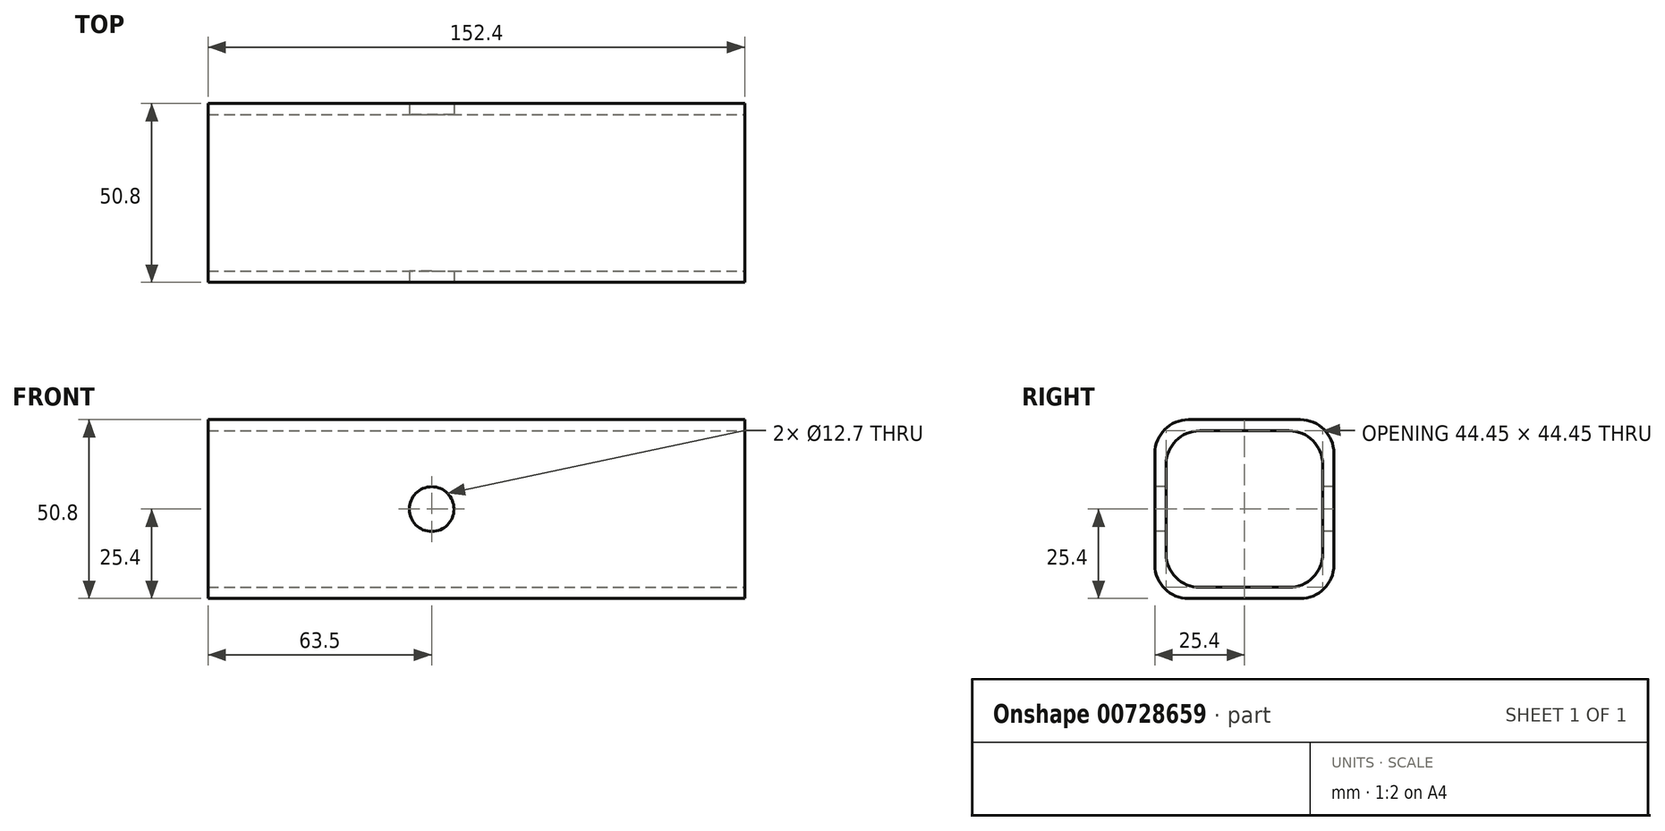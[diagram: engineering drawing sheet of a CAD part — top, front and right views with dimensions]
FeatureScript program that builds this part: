
annotation { "Feature Type Name" : "Feature", "Feature Type Description" : "" }
export const myFeature = defineFeature(function(context is Context, id is Id, definition is map)
    precondition{}
    {
        {
            var Q0;
            Q0=qCreatedBy(makeId("Right.planeOp"),FACE);
            var sketch = newSketch(context, id + "F0", { "sketchPlane" : qUnion([Q0])});
            skLineSegment(sketch, "E0.bottom", {"start": v(0, 0) * mm, "end": v(50.8, 0) * mm});
            skLineSegment(sketch, "E0.top", {"start": v(0, 50.8) * mm, "end": v(50.8, 50.8) * mm});
            skLineSegment(sketch, "E0.left", {"start": v(0, 0) * mm, "end": v(0, 50.8) * mm});
            skLineSegment(sketch, "E0.right", {"start": v(50.8, 0) * mm, "end": v(50.8, 50.8) * mm});
            skSolve(sketch);
        }
        {
            var Q0;
            Q0=qSketchRegion(id+"F0",true);
            extrude(context, id + "F1", {"entities" : qUnion([Q0]), "oppositeDirection" : true, "depth" : 152.4 * mm, "offsetDistance" : 25.4 * mm});
        }
        {
            var Q0;
            Q0=makeQuery(id+"F1.opExtrude","CAP_FACE",FACE,{"disambiguationData":[OSD([sQuery(id+"F0.wireOp",EDGE,"E0.bottom"),sQuery(id+"F0.wireOp",EDGE,"E0.top"),sQuery(id+"F0.wireOp",EDGE,"E0.left"),sQuery(id+"F0.wireOp",EDGE,"E0.right")])],"isStart":true});
            var sketch = newSketch(context, id + "F2", { "sketchPlane" : qUnion([Q0])});
            skLineSegment(sketch, "E1.0", {"start": v(3.17, 47.63) * mm, "end": v(47.63, 47.63) * mm});
            skLineSegment(sketch, "E1.1", {"start": v(3.17, 3.17) * mm, "end": v(3.17, 47.63) * mm});
            skLineSegment(sketch, "E1.2", {"start": v(3.17, 3.17) * mm, "end": v(47.63, 3.17) * mm});
            skLineSegment(sketch, "E1.3", {"start": v(47.63, 3.17) * mm, "end": v(47.63, 47.63) * mm});
            skSolve(sketch);
        }
        {
            var Q0;
            Q0=qSketchRegion(id+"F2",true);
            extrude(context, id + "F3", {"entities" : qUnion([Q0]), "operationType" : NewBodyOperationType.REMOVE, "oppositeDirection" : true, "depth" : 876.3 * mm, "offsetDistance" : 25.4 * mm});
        }
        {
            var Q0;
            Q0=makeQuery(id+"F3.boolean.opBoolean","COPY",EDGE,{"derivedFrom":makeQuery(id+"F3.opExtrude","SWEPT_EDGE",EDGE,{"disambiguationData":[OSD([sQuery(id+"F2.wireOp",EDGE,"E1.1"),sQuery(id+"F2.wireOp",EDGE,"E1.2")])]})});
            var Q1;
            Q1=makeQuery(id+"F3.boolean.opBoolean","COPY",EDGE,{"derivedFrom":makeQuery(id+"F3.opExtrude","SWEPT_EDGE",EDGE,{"disambiguationData":[OSD([sQuery(id+"F2.wireOp",EDGE,"E1.2"),sQuery(id+"F2.wireOp",EDGE,"E1.3")])]})});
            var Q2;
            Q2=makeQuery(id+"F3.boolean.opBoolean","COPY",EDGE,{"derivedFrom":makeQuery(id+"F3.opExtrude","SWEPT_EDGE",EDGE,{"disambiguationData":[OSD([sQuery(id+"F2.wireOp",EDGE,"E1.0"),sQuery(id+"F2.wireOp",EDGE,"E1.3")])]})});
            var Q3;
            Q3=makeQuery(id+"F3.boolean.opBoolean","COPY",EDGE,{"derivedFrom":makeQuery(id+"F3.opExtrude","SWEPT_EDGE",EDGE,{"disambiguationData":[OSD([sQuery(id+"F2.wireOp",EDGE,"E1.0"),sQuery(id+"F2.wireOp",EDGE,"E1.1")])]})});
            var Q4;
            Q4=makeQuery(id+"F1.opExtrude","SWEPT_EDGE",EDGE,{"disambiguationData":[OSD([sQuery(id+"F0.wireOp",EDGE,"E0.bottom"),sQuery(id+"F0.wireOp",EDGE,"E0.right")])]});
            var Q5;
            Q5=makeQuery(id+"F1.opExtrude","SWEPT_EDGE",EDGE,{"disambiguationData":[OSD([sQuery(id+"F0.wireOp",EDGE,"E0.top"),sQuery(id+"F0.wireOp",EDGE,"E0.right")])]});
            var Q6;
            Q6=makeQuery(id+"F1.opExtrude","SWEPT_EDGE",EDGE,{"disambiguationData":[OSD([sQuery(id+"F0.wireOp",EDGE,"E0.top"),sQuery(id+"F0.wireOp",EDGE,"E0.left")])]});
            var Q7;
            Q7=makeQuery(id+"F1.opExtrude","SWEPT_EDGE",EDGE,{"disambiguationData":[OSD([sQuery(id+"F0.wireOp",EDGE,"E0.bottom"),sQuery(id+"F0.wireOp",EDGE,"E0.left")])]});
            fillet(context, id + "F4", {"entities" : qUnion([Q0, Q1, Q2, Q3, Q4, Q5, Q6, Q7]), "radius" : 9.52 * mm, "tangentPropagation" : true, "allowEdgeOverflow" : false});
        }
        {
            var Q0;
            Q0=makeQuery(id+"F1.opExtrude","SWEPT_FACE",FACE,{"disambiguationData":[OSD([sQuery(id+"F0.wireOp",EDGE,"E0.left")])]});
            var sketch = newSketch(context, id + "F5", { "sketchPlane" : qUnion([Q0])});
            skPoint(sketch, "E2", {"position": v(-88.9, 25.4) * mm});
            skSolve(sketch);
        }
        {
            var Q0;
            Q0=sQuery(id+"F5.wireOp",VERTEX,"E2");
            var Q1;
            Q1=makeQuery(id+"F1.opExtrude","SWEPT_BODY",BODY,{"disambiguationData":[OSD([sQuery(id+"F0.wireOp",EDGE,"E0.bottom"),sQuery(id+"F0.wireOp",EDGE,"E0.top"),sQuery(id+"F0.wireOp",EDGE,"E0.left"),sQuery(id+"F0.wireOp",EDGE,"E0.right")])]});
            hole(context, id + "F6", {"style" : HoleStyle.SIMPLE, "endStyle" : HoleEndStyle.BLIND, "holeDiameter" : 12.7 * mm, "majorDiameter" : 6.35 * mm, "holeDepth" : 127 * mm, "isTappedThrough" : true, "tappedDepth" : 12.7 * mm, "tapClearance" : 3, "locations" : qUnion([Q0]), "scope" : qUnion([Q1])});
        }
    });
